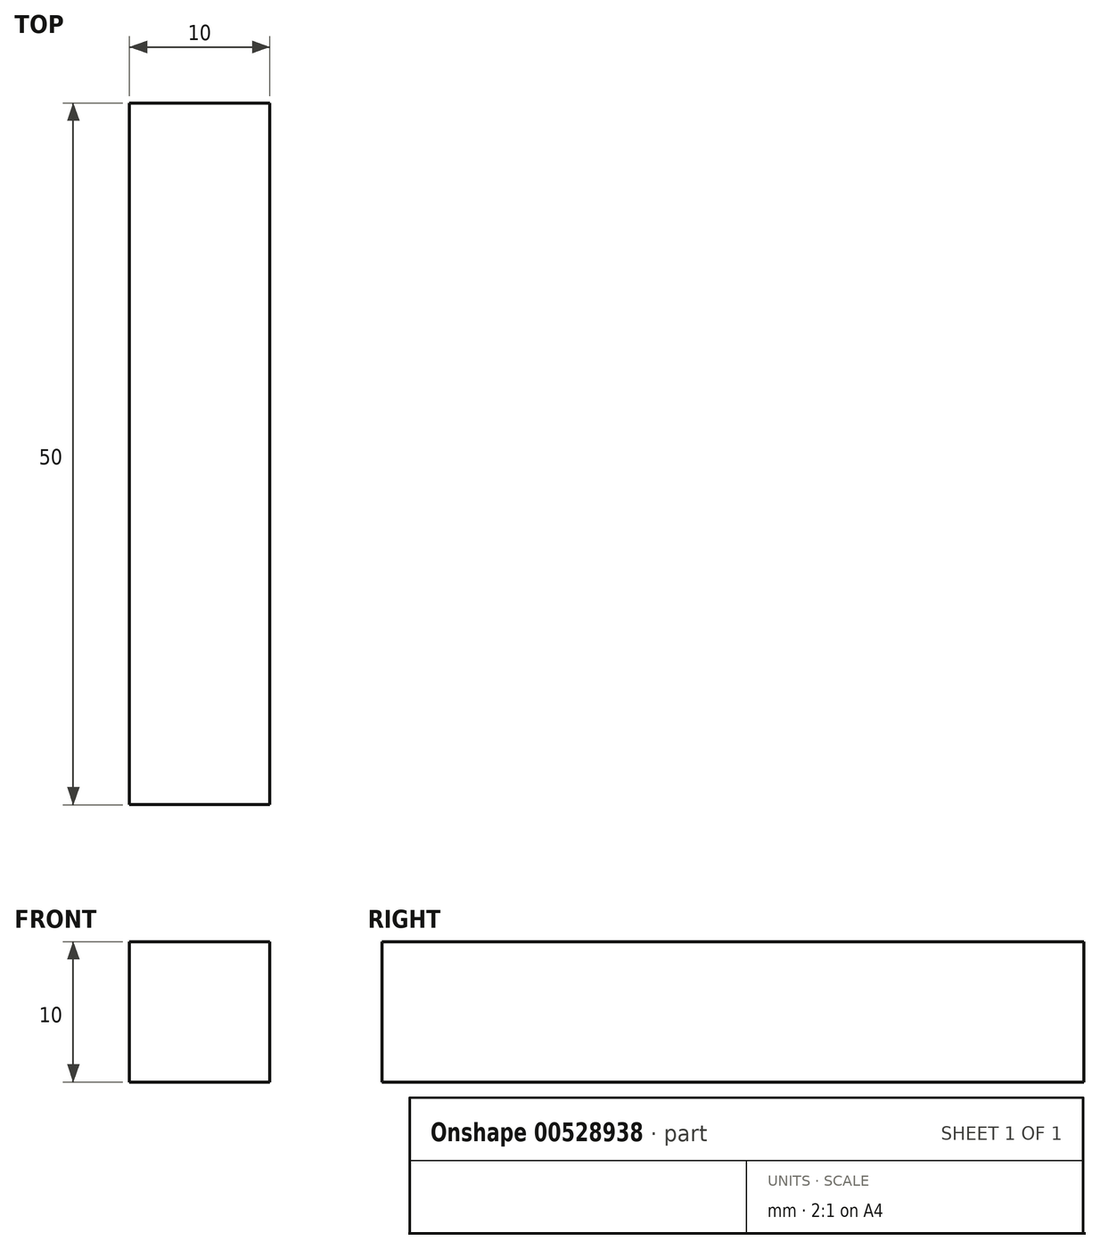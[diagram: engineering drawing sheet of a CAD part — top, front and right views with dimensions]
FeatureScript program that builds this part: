
annotation { "Feature Type Name" : "Feature", "Feature Type Description" : "" }
export const myFeature = defineFeature(function(context is Context, id is Id, definition is map)
    precondition{}
    {
        {
            var Q0;
            Q0=qCreatedBy(makeId("Top.planeOp"),FACE);
            var sketch = newSketch(context, id + "F0", { "sketchPlane" : qUnion([Q0])});
            skLineSegment(sketch, "E0.bottom", {"start": v(-59.6, 14.64) * mm, "end": v(-69.6, 14.64) * mm});
            skLineSegment(sketch, "E0.top", {"start": v(-59.6, 64.64) * mm, "end": v(-69.6, 64.64) * mm});
            skLineSegment(sketch, "E0.left", {"start": v(-59.6, 14.64) * mm, "end": v(-59.6, 64.64) * mm});
            skLineSegment(sketch, "E0.right", {"start": v(-69.6, 14.64) * mm, "end": v(-69.6, 64.64) * mm});
            skPoint(sketch, "E0.middle", {"position": v(-64.6, 39.64) * mm});
            skSolve(sketch);
        }
        {
            var Q0;
            Q0=makeQuery(id+"F0.imprint","IMPRINT",FACE,{"disambiguationData":[TD([[makeQuery(id+"F0.imprint","IMPRINT",EDGE,{"derivedFrom":sQuery(id+"F0.wireOp",EDGE,"E0.bottom")}),-1.0]])]});
            extrude(context, id + "F1", {"entities" : qUnion([Q0]), "depth" : 10 * mm, "offsetDistance" : 25 * mm});
        }
    });
